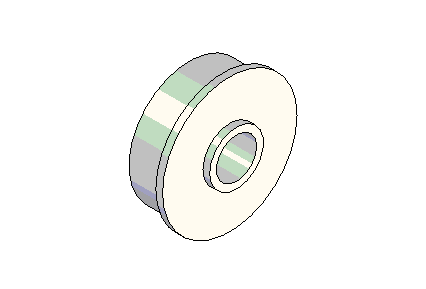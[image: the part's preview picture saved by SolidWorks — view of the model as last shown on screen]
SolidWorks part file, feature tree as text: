
SOLIDWORKS PART (.sldprt)
format: sldprt  version: not decoded by parser v0  size: 127,488 bytes
history: native  units: mm
features: sketch x4, extrude x3, cut_extrude x1 (+11 scaffold rows collapsed)
feature tree (19):
  scaffold x11  (default folders/planes/origin — collapsed)
  sketch  "Sketch1"  dims[D1=28.575mm]
  extrude  "Extrude1"  Depth=7.9375mm
  sketch  "Sketch2"  dims[D1=31.75mm]
  extrude  "Extrude2"  Depth=1.5875mm
  sketch  "Sketch3"  dims[D1=12.7mm]
  extrude  "Extrude3"  Depth=1.5875mm
  sketch  "Sketch4"  dims[D1=9.525mm]
  cut_extrude  "Cut-Extrude1"  [1 undecoded]
decode coverage: 7 of 8 modeling features carry decoded parameters
note: 1 parameter value undecoded
note: suppression state not decoded; provenance and decode notes live in map.json
